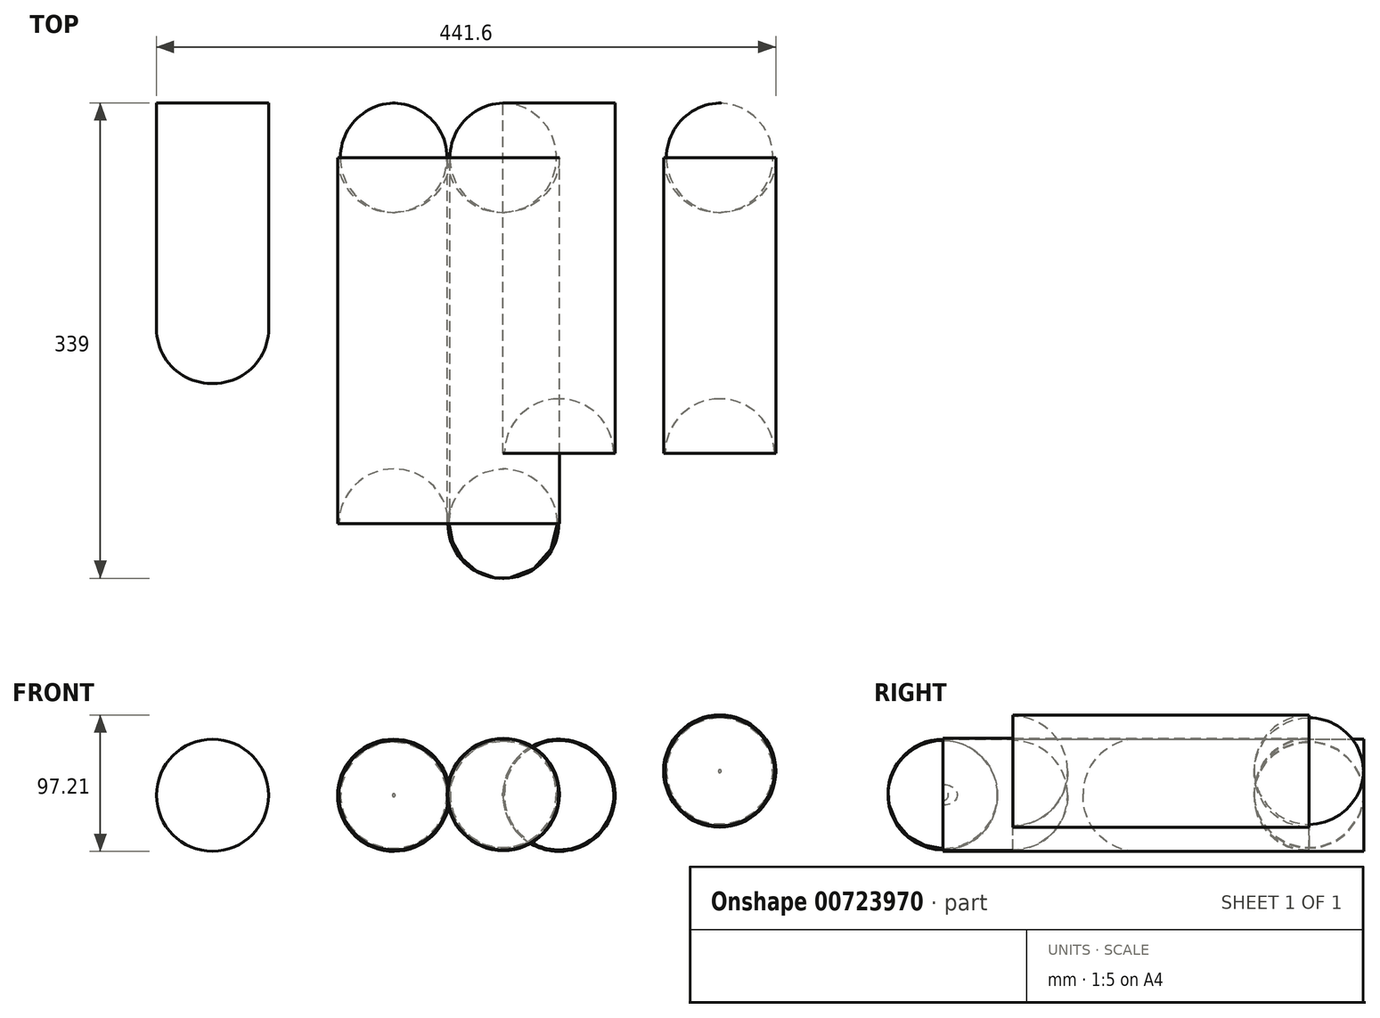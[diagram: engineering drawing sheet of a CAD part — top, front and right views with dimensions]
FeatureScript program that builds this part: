
annotation { "Feature Type Name" : "Feature", "Feature Type Description" : "" }
export const myFeature = defineFeature(function(context is Context, id is Id, definition is map)
    precondition{}
    {
        {
            var Q0;
            Q0=qCreatedBy(makeId("Front.planeOp"),FACE);
            var sketch = newSketch(context, id + "F0", { "sketchPlane" : qUnion([Q0])});
            skCircle(sketch, "E0", {"center": v(-150.13, 18.27) * mm, "radius": 40 * mm});
            skCircle(sketch, "E1", {"center": v(-20.96, 18.27) * mm, "radius": 40 * mm});
            skCircle(sketch, "E2", {"center": v(96.88, 18.27) * mm, "radius": 40 * mm});
            skSolve(sketch);
        }
        {
            var Q0;
            Q0=makeQuery(id+"F0.imprint","IMPRINT",FACE,{"disambiguationData":[TD([[makeQuery(id+"F0.imprint","IMPRINT",EDGE,{"derivedFrom":sQuery(id+"F0.wireOp",EDGE,"E0")}),1.0]])]});
            extrude(context, id + "F1", {"entities" : qUnion([Q0]), "depth" : 200 * mm, "offsetDistance" : 25 * mm});
        }
        {
            var Q0;
            Q0=makeQuery(id+"F0.imprint","IMPRINT",FACE,{"disambiguationData":[TD([[makeQuery(id+"F0.imprint","IMPRINT",EDGE,{"derivedFrom":sQuery(id+"F0.wireOp",EDGE,"E1")}),1.0]])]});
            extrude(context, id + "F2", {"entities" : qUnion([Q0]), "depth" : 300 * mm, "offsetDistance" : 25 * mm});
        }
        {
            var Q0;
            Q0=makeQuery(id+"F0.imprint","IMPRINT",FACE,{"disambiguationData":[TD([[makeQuery(id+"F0.imprint","IMPRINT",EDGE,{"derivedFrom":sQuery(id+"F0.wireOp",EDGE,"E2")}),1.0]])]});
            extrude(context, id + "F3", {"entities" : qUnion([Q0]), "depth" : 250 * mm, "offsetDistance" : 25 * mm});
        }
        {
            var Q0;
            Q0=makeQuery(id+"F1.opExtrude","CAP_EDGE",EDGE,{"disambiguationData":[OSD([sQuery(id+"F0.wireOp",EDGE,"E0")])],"isStart":false});
            fillet(context, id + "F4", {"entities" : qUnion([Q0]), "radius" : 39 * mm, "tangentPropagation" : true, "allowEdgeOverflow" : false});
        }
        {
            var Q0;
            Q0=makeQuery(id+"F2.opExtrude","CAP_FACE",FACE,{"disambiguationData":[OSD([sQuery(id+"F0.wireOp",EDGE,"E1")])],"isStart":false});
            var sketch = newSketch(context, id + "F5", { "sketchPlane" : qUnion([Q0])});
            skCircle(sketch, "E3", {"center": v(-20.96, 18.27) * mm, "radius": 39 * mm});
            skSolve(sketch);
        }
        {
            var Q0;
            Q0=makeQuery(id+"F5.imprint","IMPRINT",FACE,{"disambiguationData":[TD([[makeQuery(id+"F5.imprint","IMPRINT",EDGE,{"derivedFrom":sQuery(id+"F5.wireOp",EDGE,"E3")}),1.0]])]});
            extrude(context, id + "F6", {"entities" : qUnion([Q0]), "operationType" : NewBodyOperationType.REMOVE, "oppositeDirection" : true, "depth" : 39 * mm, "offsetDistance" : 25 * mm});
        }
        {
            var Q0;
            Q0=makeQuery(id+"F6.boolean.opBoolean","COPY",EDGE,{"derivedFrom":makeQuery(id+"F6.opExtrude","CAP_EDGE",EDGE,{"disambiguationData":[OSD([sQuery(id+"F5.wireOp",EDGE,"E3")])],"isStart":false})});
            fillet(context, id + "F7", {"entities" : qUnion([Q0]), "radius" : 39 * mm, "tangentPropagation" : true, "allowEdgeOverflow" : false});
        }
        {
            var Q0;
            Q0=makeQuery(id+"F2.opExtrude","CAP_EDGE",EDGE,{"disambiguationData":[OSD([sQuery(id+"F0.wireOp",EDGE,"E1")])],"isStart":true});
            fillet(context, id + "F8", {"entities" : qUnion([Q0]), "radius" : 39 * mm, "tangentPropagation" : true, "allowEdgeOverflow" : false});
        }
        {
            var Q0;
            Q0=makeQuery(id+"F3.opExtrude","CAP_FACE",FACE,{"disambiguationData":[OSD([sQuery(id+"F0.wireOp",EDGE,"E2")])],"isStart":false});
            var sketch = newSketch(context, id + "F9", { "sketchPlane" : qUnion([Q0])});
            skCircle(sketch, "E4", {"center": v(96.88, 18.27) * mm, "radius": 39 * mm});
            skSolve(sketch);
        }
        {
            var Q0;
            Q0 = qSketchRegion(id + "F9", true);
            extrude(context, id + "F10", {"entities" : qUnion([Q0]), "operationType" : NewBodyOperationType.REMOVE, "oppositeDirection" : true, "depth" : 39 * mm, "offsetDistance" : 25 * mm});
        }
        {
            var Q0;
            Q0=makeQuery(id+"F10.boolean.opBoolean","COPY",EDGE,{"derivedFrom":makeQuery(id+"F10.opExtrude","CAP_EDGE",EDGE,{"disambiguationData":[OSD([sQuery(id+"F9.wireOp",EDGE,"E4")])],"isStart":false})});
            fillet(context, id + "F11", {"entities" : qUnion([Q0]), "radius" : 39 * mm, "tangentPropagation" : true, "allowEdgeOverflow" : false});
        }
        {
            var Q0;
            Q0=qCreatedBy(makeId("Front.planeOp"),FACE);
            var sketch = newSketch(context, id + "F12", { "sketchPlane" : qUnion([Q0])});
            skCircle(sketch, "E5", {"center": v(57.12, 18.84) * mm, "radius": 40 * mm});
            skSolve(sketch);
        }
        {
            var Q0;
            Q0 = qSketchRegion(id + "F12", true);
            extrude(context, id + "F13", {"entities" : qUnion([Q0]), "depth" : 300 * mm, "offsetDistance" : 25 * mm});
        }
        {
            var Q0;
            Q0=makeQuery(id+"F13.opExtrude","CAP_FACE",FACE,{"disambiguationData":[OSD([sQuery(id+"F12.wireOp",EDGE,"E5")])],"isStart":false});
            var sketch = newSketch(context, id + "F14", { "sketchPlane" : qUnion([Q0])});
            skCircle(sketch, "E6", {"center": v(57.12, 18.84) * mm, "radius": 39.5 * mm});
            skSolve(sketch);
        }
        {
            var Q0;
            Q0 = qSketchRegion(id + "F14", true);
            extrude(context, id + "F15", {"entities" : qUnion([Q0]), "operationType" : NewBodyOperationType.REMOVE, "oppositeDirection" : true, "depth" : 39 * mm, "offsetDistance" : 25 * mm});
        }
        {
            var Q0;
            Q0=makeQuery(id+"F15.boolean.opBoolean","COPY",EDGE,{"derivedFrom":makeQuery(id+"F15.opExtrude","CAP_EDGE",EDGE,{"disambiguationData":[OSD([sQuery(id+"F14.wireOp",EDGE,"E6")])],"isStart":false})});
            fillet(context, id + "F16", {"entities" : qUnion([Q0]), "radius" : 39 * mm, "tangentPropagation" : true, "allowEdgeOverflow" : false});
        }
        {
            var Q0;
            Q0=makeQuery(id+"F13.opExtrude","CAP_EDGE",EDGE,{"disambiguationData":[OSD([sQuery(id+"F12.wireOp",EDGE,"E5")])],"isStart":true});
            fillet(context, id + "F17", {"entities" : qUnion([Q0]), "radius" : 39 * mm, "tangentPropagation" : true, "allowEdgeOverflow" : false});
        }
        {
            var Q0;
            Q0=qCreatedBy(makeId("Front.planeOp"),FACE);
            var sketch = newSketch(context, id + "F18", { "sketchPlane" : qUnion([Q0])});
            skCircle(sketch, "E7", {"center": v(211.47, 35.48) * mm, "radius": 40 * mm});
            skSolve(sketch);
        }
        {
            var Q0;
            Q0 = qSketchRegion(id + "F18", true);
            extrude(context, id + "F19", {"entities" : qUnion([Q0]), "depth" : 250 * mm, "offsetDistance" : 25 * mm});
        }
        {
            var Q0;
            Q0=makeQuery(id+"F19.opExtrude","CAP_EDGE",EDGE,{"disambiguationData":[OSD([sQuery(id+"F18.wireOp",EDGE,"E7")])],"isStart":true});
            fillet(context, id + "F20", {"entities" : qUnion([Q0]), "radius" : 39 * mm, "tangentPropagation" : true, "allowEdgeOverflow" : false});
        }
        {
            var Q0;
            Q0=makeQuery(id+"F19.opExtrude","CAP_FACE",FACE,{"disambiguationData":[OSD([sQuery(id+"F18.wireOp",EDGE,"E7")])],"isStart":false});
            var sketch = newSketch(context, id + "F21", { "sketchPlane" : qUnion([Q0])});
            skCircle(sketch, "E8", {"center": v(211.47, 35.48) * mm, "radius": 39 * mm});
            skSolve(sketch);
        }
        {
            var Q0;
            Q0 = qSketchRegion(id + "F21", true);
            extrude(context, id + "F22", {"entities" : qUnion([Q0]), "operationType" : NewBodyOperationType.REMOVE, "oppositeDirection" : true, "depth" : 39 * mm, "offsetDistance" : 25 * mm});
        }
        {
            var Q0;
            Q0=makeQuery(id+"F22.boolean.opBoolean","COPY",FACE,{"derivedFrom":makeQuery(id+"F22.opExtrude","CAP_FACE",FACE,{"disambiguationData":[OSD([sQuery(id+"F21.wireOp",EDGE,"E8")])],"isStart":false})});
            fillet(context, id + "F23", {"entities" : qUnion([Q0]), "radius" : 39 * mm, "tangentPropagation" : true, "allowEdgeOverflow" : false});
        }
    });
